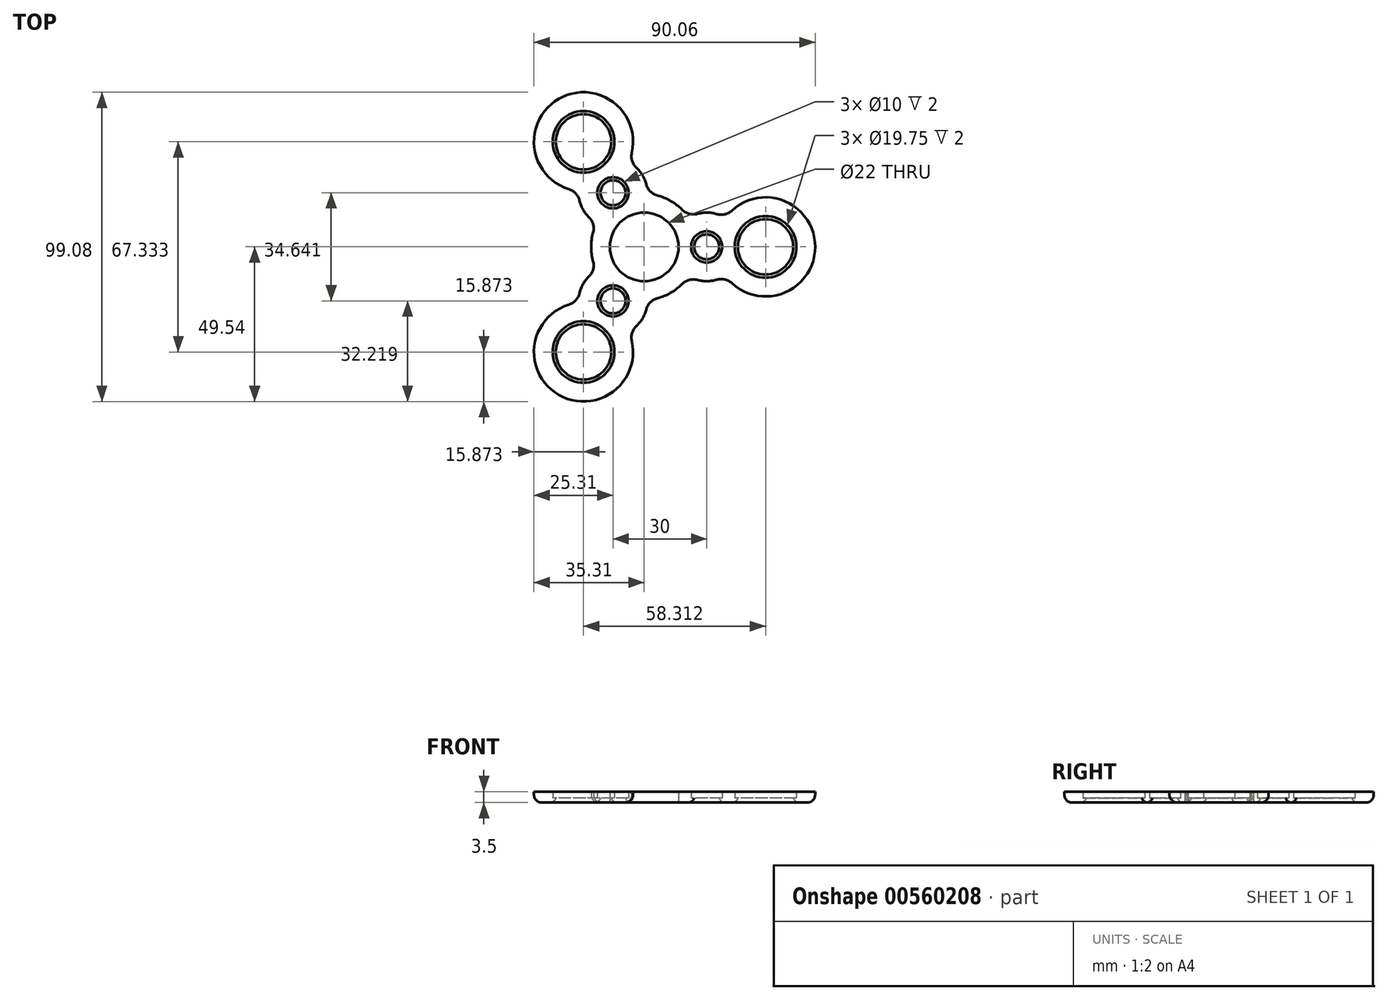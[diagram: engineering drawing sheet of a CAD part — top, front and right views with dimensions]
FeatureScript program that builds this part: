
annotation { "Feature Type Name" : "Feature", "Feature Type Description" : "" }
export const myFeature = defineFeature(function(context is Context, id is Id, definition is map)
    precondition{}
    {
        {
            var Q0;
            Q0=qCreatedBy(makeId("Top.planeOp"),FACE);
            var sketch = newSketch(context, id + "F0", { "sketchPlane" : qUnion([Q0])});
            skCircle(sketch, "E0", {"center": v(0, 0) * mm, "radius": 11 * mm});
            skCircle(sketch, "E1", {"center": v(20, 0) * mm, "radius": 5 * mm});
            skCircle(sketch, "E2", {"center": v(38.88, 0) * mm, "radius": 9.88 * mm});
            skArc(sketch, "E3.0", {"start": v(17.04, -10.6) * mm, "mid": v(20.13, -11) * mm, "end": v(23.21, -10.52) * mm});
            skArc(sketch, "E4.0", {"start": v(12.13, 11.9) * mm, "mid": v(8.5, 14.72) * mm, "end": v(4.25, 16.46) * mm});
            skArc(sketch, "E5.trimOffspring", {"start": v(23.21, 10.52) * mm, "mid": v(20.13, 11) * mm, "end": v(17.04, 10.6) * mm});
            skArc(sketch, "E6.trimOffspring", {"start": v(28.08, -11.64) * mm, "mid": v(54.75, 0) * mm, "end": v(28.08, 11.64) * mm});
            skPoint(sketch, "E7.visualSharp", {"position": v(25.97, 9.24) * mm});
            skArc(sketch, "E7.filletArc", {"start": v(23.21, 10.52) * mm, "mid": v(25.8, 10.43) * mm, "end": v(28.08, 11.64) * mm});
            skPoint(sketch, "E8.visualSharp", {"position": v(25.97, -9.24) * mm});
            skArc(sketch, "E8.filletArc", {"start": v(28.08, -11.64) * mm, "mid": v(25.8, -10.43) * mm, "end": v(23.21, -10.52) * mm});
            skPoint(sketch, "E9.visualSharp", {"position": v(14.2, -9.35) * mm});
            skArc(sketch, "E9.filletArc", {"start": v(17.04, -10.6) * mm, "mid": v(14.4, -10.58) * mm, "end": v(12.13, -11.9) * mm});
            skPoint(sketch, "E10.visualSharp", {"position": v(14.2, 9.35) * mm});
            skArc(sketch, "E10.filletArc", {"start": v(12.13, 11.9) * mm, "mid": v(14.4, 10.58) * mm, "end": v(17.04, 10.6) * mm});
            skLineSegment(sketch, "E11", {"start": v(0, 0) * mm, "end": v(-34.2, 59.22) * mm, "construction": true});
            skLineSegment(sketch, "E12", {"start": v(0, 0) * mm, "end": v(-43.63, -75.58) * mm, "construction": true});
            skCircle(sketch, "E13", {"center": v(-19.44, 33.67) * mm, "radius": 9.88 * mm});
            skCircle(sketch, "E14", {"center": v(-19.44, -33.67) * mm, "radius": 9.88 * mm});
            skArc(sketch, "E15.0", {"start": v(-3.96, 30.13) * mm, "mid": v(-27.37, 47.41) * mm, "end": v(-24.12, 18.5) * mm});
            skArc(sketch, "E16.0", {"start": v(-24.12, -18.5) * mm, "mid": v(-27.37, -47.41) * mm, "end": v(-3.96, -30.13) * mm});
            skCircle(sketch, "E17", {"center": v(-10, 17.32) * mm, "radius": 5 * mm});
            skCircle(sketch, "E18", {"center": v(-10, -17.32) * mm, "radius": 5 * mm});
            skArc(sketch, "E19.0", {"start": v(-20.72, 14.84) * mm, "mid": v(-19.6, 11.94) * mm, "end": v(-17.7, 9.46) * mm});
            skArc(sketch, "E20.0", {"start": v(-17.7, -9.46) * mm, "mid": v(-19.6, -11.94) * mm, "end": v(-20.72, -14.84) * mm});
            skArc(sketch, "E21.trimOffspring", {"start": v(0.65, 20.06) * mm, "mid": v(-0.54, 22.94) * mm, "end": v(-2.5, 25.36) * mm});
            skArc(sketch, "E22.trimOffspring", {"start": v(-16.38, 4.55) * mm, "mid": v(-17, 0) * mm, "end": v(-16.38, -4.55) * mm});
            skArc(sketch, "E23.trimOffspring", {"start": v(4.25, -16.46) * mm, "mid": v(8.5, -14.72) * mm, "end": v(12.13, -11.9) * mm});
            skArc(sketch, "E24.trimOffspring", {"start": v(-2.5, -25.36) * mm, "mid": v(-0.54, -22.94) * mm, "end": v(0.65, -20.06) * mm});
            skPoint(sketch, "E25.visualSharp", {"position": v(-4.98, 27.1) * mm});
            skArc(sketch, "E25.filletArc", {"start": v(-3.96, 30.13) * mm, "mid": v(-3.87, 27.55) * mm, "end": v(-2.5, 25.36) * mm});
            skPoint(sketch, "E26.visualSharp", {"position": v(1, 16.97) * mm});
            skArc(sketch, "E26.filletArc", {"start": v(0.65, 20.06) * mm, "mid": v(1.96, 17.77) * mm, "end": v(4.25, 16.46) * mm});
            skPoint(sketch, "E27.visualSharp", {"position": v(-20.99, 17.87) * mm});
            skArc(sketch, "E27.filletArc", {"start": v(-20.72, 14.84) * mm, "mid": v(-21.93, 17.12) * mm, "end": v(-24.12, 18.5) * mm});
            skPoint(sketch, "E28.visualSharp", {"position": v(-15.2, 7.62) * mm});
            skArc(sketch, "E28.filletArc", {"start": v(-16.38, 4.55) * mm, "mid": v(-16.37, 7.19) * mm, "end": v(-17.7, 9.46) * mm});
            skPoint(sketch, "E29.visualSharp", {"position": v(-15.2, -7.62) * mm});
            skArc(sketch, "E29.filletArc", {"start": v(-17.7, -9.46) * mm, "mid": v(-16.37, -7.19) * mm, "end": v(-16.38, -4.55) * mm});
            skPoint(sketch, "E30.visualSharp", {"position": v(1, -16.97) * mm});
            skArc(sketch, "E30.filletArc", {"start": v(4.25, -16.46) * mm, "mid": v(1.96, -17.77) * mm, "end": v(0.65, -20.06) * mm});
            skPoint(sketch, "E31.visualSharp", {"position": v(-20.99, -17.87) * mm});
            skArc(sketch, "E31.filletArc", {"start": v(-24.12, -18.5) * mm, "mid": v(-21.93, -17.12) * mm, "end": v(-20.72, -14.84) * mm});
            skPoint(sketch, "E32.visualSharp", {"position": v(-4.98, -27.1) * mm});
            skArc(sketch, "E32.filletArc", {"start": v(-2.5, -25.36) * mm, "mid": v(-3.87, -27.55) * mm, "end": v(-3.96, -30.13) * mm});
            skCircle(sketch, "E33.0", {"center": v(-19.44, 33.67) * mm, "radius": 8.88 * mm});
            skCircle(sketch, "E34.0", {"center": v(-10, 17.32) * mm, "radius": 4 * mm});
            skCircle(sketch, "E35.0", {"center": v(20, 0) * mm, "radius": 4 * mm});
            skCircle(sketch, "E36.0", {"center": v(38.88, 0) * mm, "radius": 8.88 * mm});
            skCircle(sketch, "E37.0", {"center": v(-10, -17.32) * mm, "radius": 4 * mm});
            skCircle(sketch, "E38.0", {"center": v(-19.44, -33.67) * mm, "radius": 8.88 * mm});
            skSolve(sketch);
        }
        {
            var Q0;
            Q0=makeQuery(id+"F0.imprint","IMPRINT",FACE,{"disambiguationData":[TD([[makeQuery(id+"F0.imprint","IMPRINT",EDGE,{"derivedFrom":sQuery(id+"F0.wireOp",EDGE,"E0")}),-1.0]])]});
            extrude(context, id + "F1", {"entities" : qUnion([Q0]), "depth" : 3.5 * mm, "offsetDistance" : 25 * mm});
        }
        {
            var Q0;
            Q0=makeQuery(id+"F0.imprint","IMPRINT",FACE,{"disambiguationData":[TD([[makeQuery(id+"F0.imprint","IMPRINT",EDGE,{"derivedFrom":sQuery(id+"F0.wireOp",EDGE,"E13")}),1.0]])]});
            var Q1;
            Q1=makeQuery(id+"F0.imprint","IMPRINT",FACE,{"disambiguationData":[TD([[makeQuery(id+"F0.imprint","IMPRINT",EDGE,{"derivedFrom":sQuery(id+"F0.wireOp",EDGE,"E2")}),1.0]])]});
            var Q2;
            Q2=makeQuery(id+"F0.imprint","IMPRINT",FACE,{"disambiguationData":[TD([[makeQuery(id+"F0.imprint","IMPRINT",EDGE,{"derivedFrom":sQuery(id+"F0.wireOp",EDGE,"E14")}),1.0]])]});
            extrude(context, id + "F2", {"entities" : qUnion([Q0, Q1, Q2]), "operationType" : NewBodyOperationType.ADD, "depth" : 1.5 * mm, "offsetDistance" : 25 * mm});
        }
        {
            var Q0;
            Q0=makeQuery(id+"F0.imprint","IMPRINT",FACE,{"disambiguationData":[TD([[makeQuery(id+"F0.imprint","IMPRINT",EDGE,{"derivedFrom":sQuery(id+"F0.wireOp",EDGE,"E1")}),1.0]])]});
            var Q1;
            Q1=makeQuery(id+"F0.imprint","IMPRINT",FACE,{"disambiguationData":[TD([[makeQuery(id+"F0.imprint","IMPRINT",EDGE,{"derivedFrom":sQuery(id+"F0.wireOp",EDGE,"E18")}),1.0]])]});
            var Q2;
            Q2=makeQuery(id+"F0.imprint","IMPRINT",FACE,{"disambiguationData":[TD([[makeQuery(id+"F0.imprint","IMPRINT",EDGE,{"derivedFrom":sQuery(id+"F0.wireOp",EDGE,"E17")}),1.0]])]});
            extrude(context, id + "F3", {"entities" : qUnion([Q0, Q1, Q2]), "operationType" : NewBodyOperationType.ADD, "depth" : 1.5 * mm, "offsetDistance" : 25 * mm});
        }
        {
            var Q0;
            Q0=makeQuery(id+"F1.opExtrude","CAP_EDGE",EDGE,{"disambiguationData":[OSD([sQuery(id+"F0.wireOp",EDGE,"E22.trimOffspring")])],"isStart":true});
            fillet(context, id + "F4", {"entities" : qUnion([Q0]), "radius" : 2.5 * mm, "tangentPropagation" : true, "allowEdgeOverflow" : false});
        }
        {
            var Q0;
            Q0=makeQuery(id+"F2.opExtrude","CAP_EDGE",EDGE,{"disambiguationData":[OSD([sQuery(id+"F0.wireOp",EDGE,"E33.0")])],"isStart":true});
            var Q1;
            Q1=makeQuery(id+"F3.opExtrude","CAP_EDGE",EDGE,{"disambiguationData":[OSD([sQuery(id+"F0.wireOp",EDGE,"E34.0")])],"isStart":true});
            var Q2;
            Q2=makeQuery(id+"F3.opExtrude","CAP_EDGE",EDGE,{"disambiguationData":[OSD([sQuery(id+"F0.wireOp",EDGE,"E35.0")])],"isStart":true});
            var Q3;
            Q3=makeQuery(id+"F2.opExtrude","CAP_EDGE",EDGE,{"disambiguationData":[OSD([sQuery(id+"F0.wireOp",EDGE,"E36.0")])],"isStart":true});
            var Q4;
            Q4=makeQuery(id+"F3.opExtrude","CAP_EDGE",EDGE,{"disambiguationData":[OSD([sQuery(id+"F0.wireOp",EDGE,"E37.0")])],"isStart":true});
            var Q5;
            Q5=makeQuery(id+"F2.opExtrude","CAP_EDGE",EDGE,{"disambiguationData":[OSD([sQuery(id+"F0.wireOp",EDGE,"E38.0")])],"isStart":true});
            fillet(context, id + "F5", {"entities" : qUnion([Q0, Q1, Q2, Q3, Q4, Q5]), "radius" : 2 * mm, "tangentPropagation" : true, "allowEdgeOverflow" : false});
        }
    });
